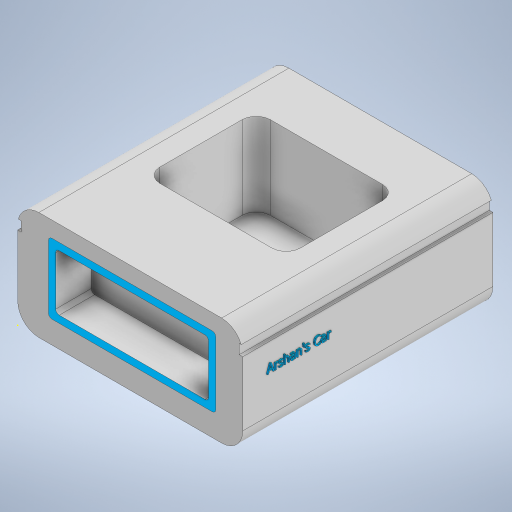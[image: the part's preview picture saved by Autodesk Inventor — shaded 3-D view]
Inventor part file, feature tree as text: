
AUTODESK INVENTOR PART (.ipt)
format: ipt  version: 2023 (Build 270158000, 158)  size: 674,304 bytes
history: native  units: in
note: dims shown in document units (in); Inventor stores cm internally (conversion verified against a paired STEP export)
features: sketch x10, extrude x8, fillet x3, emboss x1
ambient origin geometry x8: Origin, YZ Plane, XZ Plane, XY Plane, X Axis, Y Axis, Z Axis, Center Point
bodies: Solid1 (feature_tree)
feature tree (22):
  extrude  "Extrusion1"  Depth=3.548in
  extrude  "Extrusion2"  Depth=1.536in
  extrude  "Extrusion3"  Depth=1.217in
  extrude  "Extrusion4"  Depth=1.176in TaperAngle=0.0deg
  fillet  "Fillet3"  Radius=2.169in
  fillet  "Fillet6"  Radius=0.792in
  extrude  "Extrusion5"  Depth=0.504in
  fillet  "Fillet7"  Radius=0.504in
  sketch  "Sketch8"  dims[d16=2.169in d17=0.792in d18=0.419in d19=0.539in d20=0.504in d21=0.0in]
  extrude  "Extrusion6"  Depth=0.504in TaperAngle=0.0deg
  emboss  "Emboss1"
  extrude  "Extrusion10"  Depth=0.2in
  sketch  "Sketch2"  dims[d0=3.194in d1=3.548in]
  sketch  "Sketch3"  dims[d2=1.536in d3=0.0in d4=1.991in]
  sketch  "Sketch4"  dims[d5=1.566in d6=1.217in]
  sketch  "Sketch5"  dims[d7=0.602in d8=1.176in d9=0.0in d10=2.169in d11=0.792in]
  sketch  "Sketch6"  dims[d12=0.419in d13=0.539in d14=0.504in d15=0.0in]
  sketch  "Sketch9"  dims[d24=0.3in d27=0.2in]
  sketch  "Sketch12"  dims[d28=0.103in d29=0.103in]
  sketch  "Sketch15"  dims[d31=0.101in d32=0.0in d33=0.0in d34=0.05in d35=0.05in d36=0.05in d37=0.0in d38=0.02in d39=0.0in d47=0.0in d48=0.05in d49=0.05in d50=0.0in d22=0.0in d23=0.0in d25=0.0in d40=0.5in d41=0.0344in d51=0.5in d52=0.0344in]
  sketch  "Sketch14"  dims[d30=0.101in]
  extrude  "Extrusion9"  Depth=0.103in
